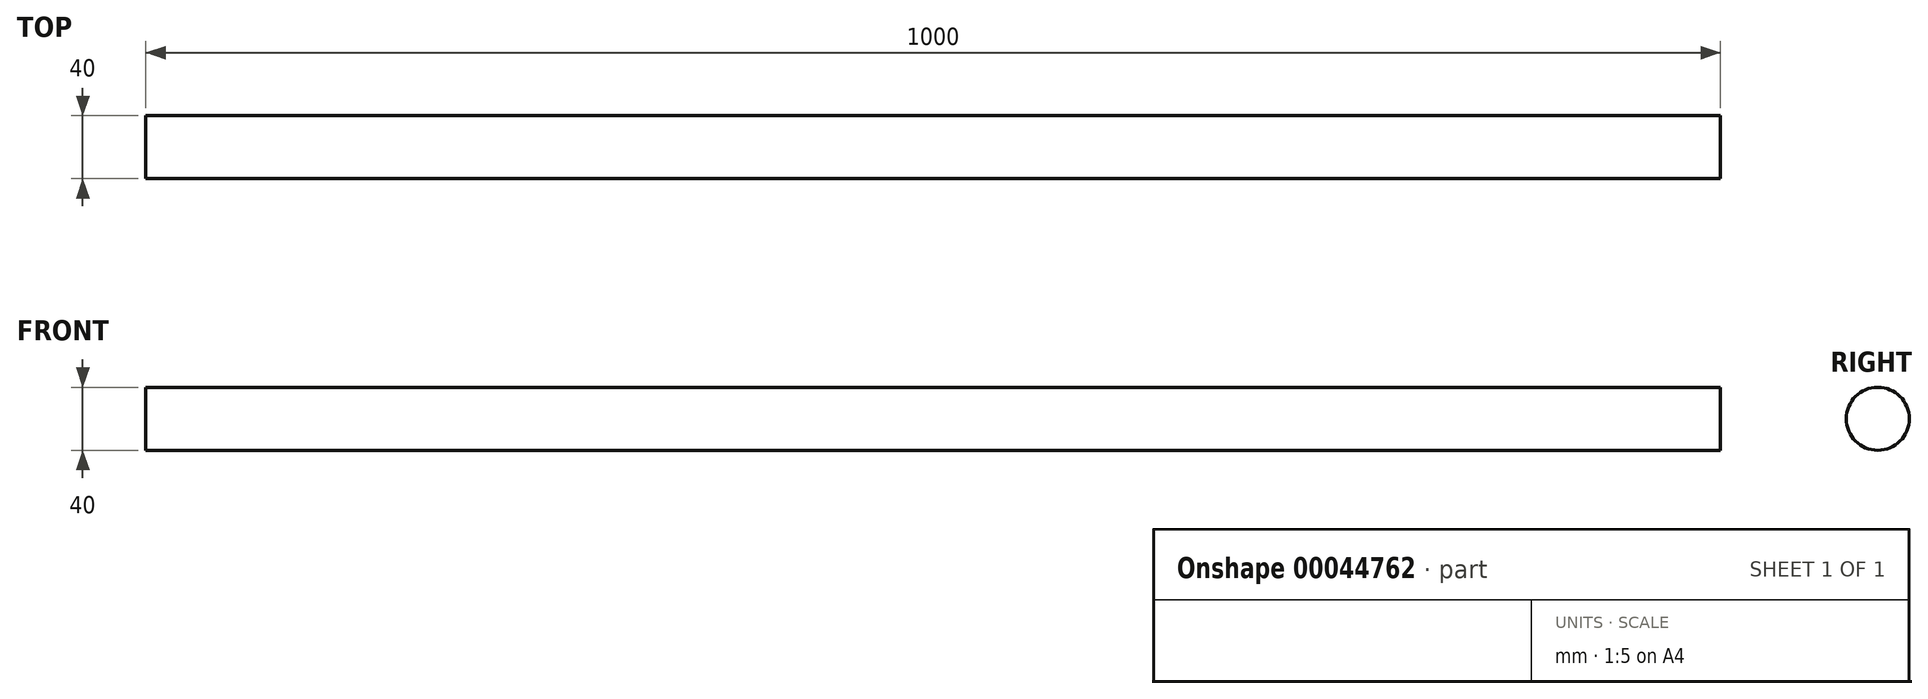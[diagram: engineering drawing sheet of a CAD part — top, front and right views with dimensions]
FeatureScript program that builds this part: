
annotation { "Feature Type Name" : "Feature", "Feature Type Description" : "" }
export const myFeature = defineFeature(function(context is Context, id is Id, definition is map)
    precondition{}
    {
        {
            var Q0;
            Q0=qCreatedBy(makeId("Right.planeOp"),FACE);
            var sketch = newSketch(context, id + "F0", { "sketchPlane" : qUnion([Q0])});
            skCircle(sketch, "E0", {"center": v(0, 0) * mm, "radius": 20 * mm});
            skSolve(sketch);
        }
        {
            var Q0;
            Q0=makeQuery(id+"F0.imprint","IMPRINT",FACE,{"disambiguationData":[TD([[makeQuery(id+"F0.imprint","IMPRINT",EDGE,{"derivedFrom":sQuery(id+"F0.wireOp",EDGE,"E0")}),1.0]])]});
            extrude(context, id + "F1", {"entities" : qUnion([Q0]), "depth" : 1000 * mm});
        }
    });
